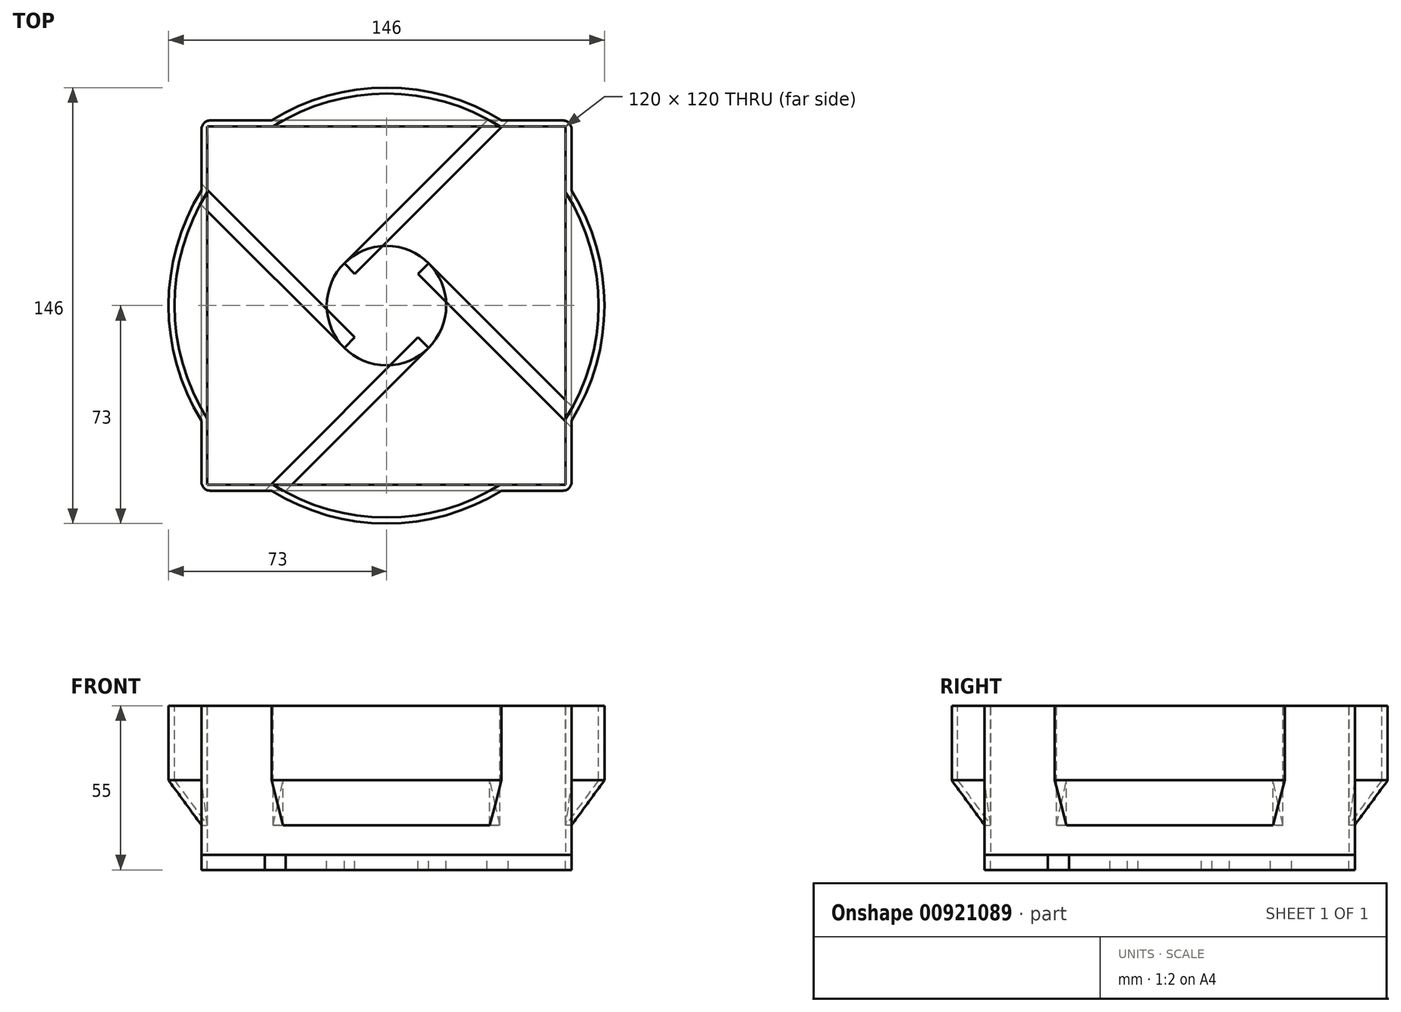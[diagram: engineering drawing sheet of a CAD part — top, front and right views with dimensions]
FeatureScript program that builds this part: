
annotation { "Feature Type Name" : "Feature", "Feature Type Description" : "" }
export const myFeature = defineFeature(function(context is Context, id is Id, definition is map)
    precondition{}
    {
        {
            var Q0;
            Q0=qCreatedBy(makeId("Top.planeOp"),FACE);
            var sketch = newSketch(context, id + "F0", { "sketchPlane" : qUnion([Q0])});
            skLineSegment(sketch, "E0.bottom", {"start": v(60, -60) * mm, "end": v(-60, -60) * mm});
            skLineSegment(sketch, "E0.top", {"start": v(60, 60) * mm, "end": v(-60, 60) * mm});
            skLineSegment(sketch, "E0.left", {"start": v(60, -60) * mm, "end": v(60, 60) * mm});
            skLineSegment(sketch, "E0.right", {"start": v(-60, -60) * mm, "end": v(-60, 60) * mm});
            skPoint(sketch, "E0.middle", {"position": v(0, 0) * mm});
            skLineSegment(sketch, "E1.bottom", {"start": v(62, -62) * mm, "end": v(-62, -62) * mm});
            skLineSegment(sketch, "E1.top", {"start": v(62, 62) * mm, "end": v(-62, 62) * mm});
            skLineSegment(sketch, "E1.left", {"start": v(62, -62) * mm, "end": v(62, 62) * mm});
            skLineSegment(sketch, "E1.right", {"start": v(-62, -62) * mm, "end": v(-62, 62) * mm});
            skCircle(sketch, "E2", {"center": v(0, 0) * mm, "radius": 20 * mm});
            skSolve(sketch);
        }
        {
            var Q0;
            Q0=makeQuery(id+"F0.imprint","IMPRINT",FACE,{"disambiguationData":[TD([[makeQuery(id+"F0.imprint","IMPRINT",EDGE,{"derivedFrom":sQuery(id+"F0.wireOp",EDGE,"E0.bottom")}),1.0]])]});
            extrude(context, id + "F1", {"entities" : qUnion([Q0]), "oppositeDirection" : true, "depth" : 5 * mm, "offsetDistance" : 25 * mm});
        }
        {
            var Q0;
            Q0=qCreatedBy(makeId("Top.planeOp"),FACE);
            var sketch = newSketch(context, id + "F2", { "sketchPlane" : qUnion([Q0])});
            skCircle(sketch, "E3", {"center": v(0, 0) * mm, "radius": 20 * mm});
            skSolve(sketch);
        }
        {
            var Q0;
            Q0=makeQuery(id+"F2.imprint","IMPRINT",FACE,{"disambiguationData":[TD([[makeQuery(id+"F2.imprint","IMPRINT",EDGE,{"derivedFrom":sQuery(id+"F2.wireOp",EDGE,"E3")}),1.0]])]});
            extrude(context, id + "F3", {"entities" : qUnion([Q0]), "oppositeDirection" : true, "depth" : 5 * mm, "offsetDistance" : 25 * mm});
        }
        {
            var Q0;
            Q0=qCreatedBy(makeId("Top.planeOp"),FACE);
            var sketch = newSketch(context, id + "F4", { "sketchPlane" : qUnion([Q0])});
            skLineSegment(sketch, "E4", {"start": v(0, 0) * mm, "end": v(-10.6, 10.6) * mm});
            skLineSegment(sketch, "E5", {"start": v(-10.6, 10.6) * mm, "end": v(-14.14, 14.14) * mm});
            skLineSegment(sketch, "E6", {"start": v(-14.14, 14.14) * mm, "end": v(33.72, 62) * mm});
            skLineSegment(sketch, "E7", {"start": v(-10.6, 10.6) * mm, "end": v(40.79, 62) * mm});
            skLineSegment(sketch, "E8", {"start": v(33.72, 62) * mm, "end": v(40.79, 62) * mm});
            skLineSegment(sketch, "E9.1.0", {"start": v(-14.14, -14.14) * mm, "end": v(-62, 33.72) * mm});
            skLineSegment(sketch, "E9.1.1", {"start": v(-62, 33.72) * mm, "end": v(-62, 40.79) * mm});
            skLineSegment(sketch, "E9.1.2", {"start": v(-10.6, -10.6) * mm, "end": v(-62, 40.79) * mm});
            skLineSegment(sketch, "E9.1.3", {"start": v(-10.6, -10.6) * mm, "end": v(-14.14, -14.14) * mm});
            skLineSegment(sketch, "E9.2.0", {"start": v(14.14, -14.14) * mm, "end": v(-33.72, -62) * mm});
            skLineSegment(sketch, "E9.2.1", {"start": v(-33.72, -62) * mm, "end": v(-40.79, -62) * mm});
            skLineSegment(sketch, "E9.2.2", {"start": v(10.6, -10.6) * mm, "end": v(-40.79, -62) * mm});
            skLineSegment(sketch, "E9.2.3", {"start": v(10.6, -10.6) * mm, "end": v(14.14, -14.14) * mm});
            skLineSegment(sketch, "E9.3.0", {"start": v(14.14, 14.14) * mm, "end": v(62, -33.72) * mm});
            skLineSegment(sketch, "E9.3.1", {"start": v(62, -33.72) * mm, "end": v(62, -40.79) * mm});
            skLineSegment(sketch, "E9.3.2", {"start": v(10.6, 10.6) * mm, "end": v(62, -40.79) * mm});
            skLineSegment(sketch, "E9.3.3", {"start": v(10.6, 10.6) * mm, "end": v(14.14, 14.14) * mm});
            skPoint(sketch, "E9.center", {"position": v(0, 0) * mm});
            skSolve(sketch);
        }
        {
            var Q0;
            Q0=makeQuery(id+"F4.imprint","IMPRINT",FACE,{"disambiguationData":[TD([[makeQuery(id+"F4.imprint","IMPRINT",EDGE,{"derivedFrom":sQuery(id+"F4.wireOp",EDGE,"E9.1.0")}),-1.0]])]});
            var Q1;
            Q1=makeQuery(id+"F4.imprint","IMPRINT",FACE,{"disambiguationData":[TD([[makeQuery(id+"F4.imprint","IMPRINT",EDGE,{"derivedFrom":sQuery(id+"F4.wireOp",EDGE,"E5")}),-1.0]])]});
            var Q2;
            Q2=makeQuery(id+"F4.imprint","IMPRINT",FACE,{"disambiguationData":[TD([[makeQuery(id+"F4.imprint","IMPRINT",EDGE,{"derivedFrom":sQuery(id+"F4.wireOp",EDGE,"E9.3.0")}),-1.0]])]});
            var Q3;
            Q3=makeQuery(id+"F4.imprint","IMPRINT",FACE,{"disambiguationData":[TD([[makeQuery(id+"F4.imprint","IMPRINT",EDGE,{"derivedFrom":sQuery(id+"F4.wireOp",EDGE,"E9.2.0")}),-1.0]])]});
            extrude(context, id + "F5", {"entities" : qUnion([Q0, Q1, Q2, Q3]), "oppositeDirection" : true, "depth" : 5 * mm, "offsetDistance" : 25 * mm});
        }
        {
            var Q0;
            Q0=makeQuery(id+"F1.opExtrude","CAP_FACE",FACE,{"disambiguationData":[OSD([sQuery(id+"F0.wireOp",EDGE,"E0.bottom"),sQuery(id+"F0.wireOp",EDGE,"E0.top"),sQuery(id+"F0.wireOp",EDGE,"E0.left"),sQuery(id+"F0.wireOp",EDGE,"E0.right"),sQuery(id+"F0.wireOp",EDGE,"E1.bottom"),sQuery(id+"F0.wireOp",EDGE,"E1.top"),sQuery(id+"F0.wireOp",EDGE,"E1.left"),sQuery(id+"F0.wireOp",EDGE,"E1.right")])],"isStart":true});
            extrude(context, id + "F6", {"entities" : qUnion([Q0]), "depth" : 50 * mm, "offsetDistance" : 25 * mm});
        }
        {
            var Q0;
            Q0=makeQuery(id+"F6.opExtrude","CAP_FACE",FACE,{"disambiguationData":[OSD([sQuery(id+"F0.wireOp",EDGE,"E0.bottom"),sQuery(id+"F0.wireOp",EDGE,"E0.top"),sQuery(id+"F0.wireOp",EDGE,"E0.left"),sQuery(id+"F0.wireOp",EDGE,"E0.right"),sQuery(id+"F0.wireOp",EDGE,"E1.bottom"),sQuery(id+"F0.wireOp",EDGE,"E1.top"),sQuery(id+"F0.wireOp",EDGE,"E1.left"),sQuery(id+"F0.wireOp",EDGE,"E1.right")])],"isStart":false});
            var sketch = newSketch(context, id + "F7", { "sketchPlane" : qUnion([Q0])});
            skCircle(sketch, "E10", {"center": v(0, 0) * mm, "radius": 71 * mm});
            skCircle(sketch, "E11", {"center": v(0, 0) * mm, "radius": 73 * mm});
            skLineSegment(sketch, "E12", {"start": v(34.6, -62) * mm, "end": v(-34.6, -62) * mm});
            skLineSegment(sketch, "E13", {"start": v(37.96, -60) * mm, "end": v(-37.96, -60) * mm});
            skLineSegment(sketch, "E14", {"start": v(60, -37.96) * mm, "end": v(60, 37.96) * mm});
            skLineSegment(sketch, "E15", {"start": v(62, -34.6) * mm, "end": v(62, 34.6) * mm});
            skLineSegment(sketch, "E16", {"start": v(37.96, 60) * mm, "end": v(-37.96, 60) * mm});
            skLineSegment(sketch, "E17", {"start": v(34.6, 62) * mm, "end": v(-34.6, 62) * mm});
            skLineSegment(sketch, "E18", {"start": v(-62, -34.6) * mm, "end": v(-62, 34.6) * mm});
            skLineSegment(sketch, "E19", {"start": v(-60, -37.96) * mm, "end": v(-60, 37.96) * mm});
            skLineSegment(sketch, "E20", {"start": v(-37.96, -60) * mm, "end": v(-41.58, -60) * mm});
            skLineSegment(sketch, "E21", {"start": v(-60, -37.96) * mm, "end": v(-60, -41.58) * mm});
            skLineSegment(sketch, "E22", {"start": v(-60, 41.58) * mm, "end": v(-60, 37.96) * mm});
            skLineSegment(sketch, "E23", {"start": v(-37.96, 60) * mm, "end": v(-41.58, 60) * mm});
            skLineSegment(sketch, "E24", {"start": v(37.96, -60) * mm, "end": v(41.58, -60) * mm});
            skLineSegment(sketch, "E25", {"start": v(60, -37.96) * mm, "end": v(60, -41.58) * mm});
            skLineSegment(sketch, "E26", {"start": v(60, 37.96) * mm, "end": v(60, 41.58) * mm});
            skLineSegment(sketch, "E27", {"start": v(37.96, 60) * mm, "end": v(41.58, 60) * mm});
            skSolve(sketch);
        }
        {
            var Q0;
            Q0 = qSketchRegion(id + "F7", true);
            extrude(context, id + "F8", {"entities" : qUnion([Q0]), "operationType" : NewBodyOperationType.ADD, "oppositeDirection" : true, "depth" : 25 * mm, "offsetDistance" : 25 * mm});
        }
        {
            var Q0;
            {var subQ0=sQuery(id+"F7.wireOp",EDGE,"E12");Q0=makeQuery(id+"F7.imprint","IMPRINT",FACE,{"disambiguationData":[TD([[makeQuery(id+"F7.imprint","IMPRINT",EDGE,{"derivedFrom":subQ0}),-1.0]])]});}
            var Q1;
            {var subQ0=sQuery(id+"F7.wireOp",EDGE,"E18");Q1=makeQuery(id+"F7.imprint","IMPRINT",FACE,{"disambiguationData":[TD([[makeQuery(id+"F7.imprint","IMPRINT",EDGE,{"derivedFrom":subQ0}),-1.0]])]});}
            var Q2;
            {var subQ0=sQuery(id+"F7.wireOp",EDGE,"E16");Q2=makeQuery(id+"F7.imprint","IMPRINT",FACE,{"disambiguationData":[TD([[makeQuery(id+"F7.imprint","IMPRINT",EDGE,{"derivedFrom":subQ0}),-1.0]])]});}
            var Q3;
            {var subQ0=sQuery(id+"F7.wireOp",EDGE,"E14");Q3=makeQuery(id+"F7.imprint","IMPRINT",FACE,{"disambiguationData":[TD([[makeQuery(id+"F7.imprint","IMPRINT",EDGE,{"derivedFrom":subQ0}),-1.0]])]});}
            extrude(context, id + "F9", {"entities" : qUnion([Q0, Q1, Q2, Q3]), "operationType" : NewBodyOperationType.REMOVE, "oppositeDirection" : true, "depth" : 25 * mm, "offsetDistance" : 25 * mm});
        }
        {
            var Q0;
            Q0=makeQuery(id+"F9.boolean.opBoolean","COPY",FACE,{"derivedFrom":makeQuery(id+"F9.opExtrude","CAP_FACE",FACE,{"disambiguationData":[OSD([sQuery(id+"F7.wireOp",EDGE,"E10"),sQuery(id+"F7.wireOp",EDGE,"E14"),sQuery(id+"F7.wireOp",EDGE,"E15")])],"isStart":false})});
            var Q1;
            Q1=makeQuery(id+"F9.boolean.opBoolean","COPY",FACE,{"derivedFrom":makeQuery(id+"F9.opExtrude","CAP_FACE",FACE,{"disambiguationData":[OSD([sQuery(id+"F7.wireOp",EDGE,"E10"),sQuery(id+"F7.wireOp",EDGE,"E12"),sQuery(id+"F7.wireOp",EDGE,"E13")])],"isStart":false})});
            var Q2;
            Q2=makeQuery(id+"F9.boolean.opBoolean","COPY",FACE,{"derivedFrom":makeQuery(id+"F9.opExtrude","CAP_FACE",FACE,{"disambiguationData":[OSD([sQuery(id+"F7.wireOp",EDGE,"E10"),sQuery(id+"F7.wireOp",EDGE,"E16"),sQuery(id+"F7.wireOp",EDGE,"E17")])],"isStart":false})});
            var Q3;
            Q3=makeQuery(id+"F9.boolean.opBoolean","COPY",FACE,{"derivedFrom":makeQuery(id+"F9.opExtrude","CAP_FACE",FACE,{"disambiguationData":[OSD([sQuery(id+"F7.wireOp",EDGE,"E10"),sQuery(id+"F7.wireOp",EDGE,"E18"),sQuery(id+"F7.wireOp",EDGE,"E19")])],"isStart":false})});
            extrude(context, id + "F10", {"entities" : qUnion([Q0, Q1, Q2, Q3]), "operationType" : NewBodyOperationType.REMOVE, "oppositeDirection" : true, "depth" : 15 * mm, "offsetDistance" : 25 * mm});
        }
        {
            var Q1;
            {var subQ0=sQuery(id+"F7.wireOp",EDGE,"E10");var subQ1=sQuery(id+"F7.wireOp",EDGE,"E11");Q1=makeQuery(id+"F8.boolean.opBoolean","SPLIT",FACE,{"disambiguationData":[TD([makeQuery(id+"F6.opExtrude","SWEPT_FACE",FACE,{"disambiguationData":[OSD([sQuery(id+"F0.wireOp",EDGE,"E1.top")])]}),makeQuery(id+"F8.opExtrude","SWEPT_FACE",FACE,{"disambiguationData":[OSD([subQ0])]}),makeQuery(id+"F8.opExtrude","SWEPT_FACE",FACE,{"disambiguationData":[OSD([subQ1])]})])],"derivedFrom":makeQuery(id+"F8.opExtrude","CAP_FACE",FACE,{"disambiguationData":[OSD([subQ0,subQ1])],"isStart":false})});}
            var Q2;
            Q2=makeQuery(id+"F10.boolean.opBoolean","COPY",FACE,{"derivedFrom":makeQuery(id+"F10.opExtrude","CAP_FACE",FACE,{"disambiguationData":[OSD([sQuery(id+"F7.wireOp",EDGE,"E10"),sQuery(id+"F7.wireOp",EDGE,"E16"),sQuery(id+"F7.wireOp",EDGE,"E17")])],"isStart":false})});
            loft(context, id + "F11", {"sheetProfilesArray" : [{ "sheetProfileEntities" : qUnion([Q1]) }, { "sheetProfileEntities" : qUnion([Q2]) }]});
        }
        {
            var Q1;
            Q1=makeQuery(id+"F10.boolean.opBoolean","COPY",FACE,{"derivedFrom":makeQuery(id+"F10.opExtrude","CAP_FACE",FACE,{"disambiguationData":[OSD([sQuery(id+"F7.wireOp",EDGE,"E10"),sQuery(id+"F7.wireOp",EDGE,"E18"),sQuery(id+"F7.wireOp",EDGE,"E19")])],"isStart":false})});
            var Q2;
            {var subQ0=sQuery(id+"F7.wireOp",EDGE,"E10");var subQ1=sQuery(id+"F7.wireOp",EDGE,"E11");Q2=makeQuery(id+"F8.boolean.opBoolean","SPLIT",FACE,{"disambiguationData":[TD([makeQuery(id+"F6.opExtrude","SWEPT_FACE",FACE,{"disambiguationData":[OSD([sQuery(id+"F0.wireOp",EDGE,"E1.right")])]}),makeQuery(id+"F8.opExtrude","SWEPT_FACE",FACE,{"disambiguationData":[OSD([subQ0])]}),makeQuery(id+"F8.opExtrude","SWEPT_FACE",FACE,{"disambiguationData":[OSD([subQ1])]})])],"derivedFrom":makeQuery(id+"F8.opExtrude","CAP_FACE",FACE,{"disambiguationData":[OSD([subQ0,subQ1])],"isStart":false})});}
            loft(context, id + "F12", {"sheetProfilesArray" : [{ "sheetProfileEntities" : qUnion([Q1]) }, { "sheetProfileEntities" : qUnion([Q2]) }]});
        }
        {
            var Q1;
            Q1=makeQuery(id+"F10.boolean.opBoolean","COPY",FACE,{"derivedFrom":makeQuery(id+"F10.opExtrude","CAP_FACE",FACE,{"disambiguationData":[OSD([sQuery(id+"F7.wireOp",EDGE,"E10"),sQuery(id+"F7.wireOp",EDGE,"E12"),sQuery(id+"F7.wireOp",EDGE,"E13")])],"isStart":false})});
            var Q2;
            {var subQ0=sQuery(id+"F7.wireOp",EDGE,"E10");var subQ1=sQuery(id+"F7.wireOp",EDGE,"E11");Q2=makeQuery(id+"F8.boolean.opBoolean","SPLIT",FACE,{"disambiguationData":[TD([makeQuery(id+"F6.opExtrude","SWEPT_FACE",FACE,{"disambiguationData":[OSD([sQuery(id+"F0.wireOp",EDGE,"E1.bottom")])]}),makeQuery(id+"F8.opExtrude","SWEPT_FACE",FACE,{"disambiguationData":[OSD([subQ0])]}),makeQuery(id+"F8.opExtrude","SWEPT_FACE",FACE,{"disambiguationData":[OSD([subQ1])]})])],"derivedFrom":makeQuery(id+"F8.opExtrude","CAP_FACE",FACE,{"disambiguationData":[OSD([subQ0,subQ1])],"isStart":false})});}
            loft(context, id + "F13", {"sheetProfilesArray" : [{ "sheetProfileEntities" : qUnion([Q1]) }, { "sheetProfileEntities" : qUnion([Q2]) }]});
        }
        {
            var Q1;
            {var subQ0=sQuery(id+"F7.wireOp",EDGE,"E11");var subQ1=sQuery(id+"F7.wireOp",EDGE,"E10");Q1=makeQuery(id+"F8.boolean.opBoolean","SPLIT",FACE,{"disambiguationData":[TD([makeQuery(id+"F6.opExtrude","SWEPT_FACE",FACE,{"disambiguationData":[OSD([sQuery(id+"F0.wireOp",EDGE,"E1.left")])]}),makeQuery(id+"F8.opExtrude","SWEPT_FACE",FACE,{"disambiguationData":[OSD([subQ1])]}),makeQuery(id+"F8.opExtrude","SWEPT_FACE",FACE,{"disambiguationData":[OSD([subQ0])]})])],"derivedFrom":makeQuery(id+"F8.opExtrude","CAP_FACE",FACE,{"disambiguationData":[OSD([subQ1,subQ0])],"isStart":false})});}
            var Q2;
            Q2=makeQuery(id+"F10.boolean.opBoolean","COPY",FACE,{"derivedFrom":makeQuery(id+"F10.opExtrude","CAP_FACE",FACE,{"disambiguationData":[OSD([sQuery(id+"F7.wireOp",EDGE,"E10"),sQuery(id+"F7.wireOp",EDGE,"E14"),sQuery(id+"F7.wireOp",EDGE,"E15")])],"isStart":false})});
            loft(context, id + "F14", {"sheetProfilesArray" : [{ "sheetProfileEntities" : qUnion([Q1]) }, { "sheetProfileEntities" : qUnion([Q2]) }]});
        }
        {
            var Q0;
            {var subQ0=sQuery(id+"F7.wireOp",EDGE,"E20");Q0=makeQuery(id+"F7.imprint","IMPRINT",FACE,{"disambiguationData":[TD([[makeQuery(id+"F7.imprint","IMPRINT",EDGE,{"derivedFrom":subQ0}),-1.0]])]});}
            extrude(context, id + "F15", {"entities" : qUnion([Q0]), "operationType" : NewBodyOperationType.REMOVE, "oppositeDirection" : true, "depth" : 25 * mm, "offsetDistance" : 25 * mm});
        }
        {
            var Q0;
            {var subQ2=sQuery(id+"F7.wireOp",EDGE,"E22");Q0=makeQuery(id+"F7.imprint","IMPRINT",FACE,{"disambiguationData":[TD([[makeQuery(id+"F7.imprint","IMPRINT",EDGE,{"derivedFrom":subQ2}),-1.0]])]});}
            extrude(context, id + "F16", {"entities" : qUnion([Q0]), "operationType" : NewBodyOperationType.REMOVE, "oppositeDirection" : true, "depth" : 25 * mm, "offsetDistance" : 25 * mm});
        }
        {
            var Q0;
            {var subQ0=sQuery(id+"F7.wireOp",EDGE,"E24");Q0=makeQuery(id+"F7.imprint","IMPRINT",FACE,{"disambiguationData":[TD([[makeQuery(id+"F7.imprint","IMPRINT",EDGE,{"derivedFrom":subQ0}),-1.0]])]});}
            extrude(context, id + "F17", {"entities" : qUnion([Q0]), "operationType" : NewBodyOperationType.REMOVE, "oppositeDirection" : true, "depth" : 25 * mm, "offsetDistance" : 25 * mm});
        }
        {
            var Q0;
            {var subQ0=sQuery(id+"F7.wireOp",EDGE,"E26");Q0=makeQuery(id+"F7.imprint","IMPRINT",FACE,{"disambiguationData":[TD([[makeQuery(id+"F7.imprint","IMPRINT",EDGE,{"derivedFrom":subQ0}),1.0]])]});}
            extrude(context, id + "F18", {"entities" : qUnion([Q0]), "operationType" : NewBodyOperationType.REMOVE, "oppositeDirection" : true, "depth" : 25 * mm, "offsetDistance" : 25 * mm});
        }
        {
            var Q0;
            Q0=makeQuery(id+"F6.opExtrude","SWEPT_EDGE",EDGE,{"disambiguationData":[OSD([sQuery(id+"F0.wireOp",EDGE,"E1.top"),sQuery(id+"F0.wireOp",EDGE,"E1.left")])]});
            var Q1;
            Q1=makeQuery(id+"F1.opExtrude","SWEPT_EDGE",EDGE,{"disambiguationData":[OSD([sQuery(id+"F0.wireOp",EDGE,"E1.top"),sQuery(id+"F0.wireOp",EDGE,"E1.left")])]});
            var Q2;
            Q2=makeQuery(id+"F6.opExtrude","SWEPT_EDGE",EDGE,{"disambiguationData":[OSD([sQuery(id+"F0.wireOp",EDGE,"E1.top"),sQuery(id+"F0.wireOp",EDGE,"E1.right")])]});
            var Q3;
            Q3=makeQuery(id+"F1.opExtrude","SWEPT_EDGE",EDGE,{"disambiguationData":[OSD([sQuery(id+"F0.wireOp",EDGE,"E1.top"),sQuery(id+"F0.wireOp",EDGE,"E1.right")])]});
            var Q4;
            Q4=makeQuery(id+"F6.opExtrude","SWEPT_EDGE",EDGE,{"disambiguationData":[OSD([sQuery(id+"F0.wireOp",EDGE,"E1.bottom"),sQuery(id+"F0.wireOp",EDGE,"E1.right")])]});
            var Q5;
            Q5=makeQuery(id+"F1.opExtrude","SWEPT_EDGE",EDGE,{"disambiguationData":[OSD([sQuery(id+"F0.wireOp",EDGE,"E1.bottom"),sQuery(id+"F0.wireOp",EDGE,"E1.right")])]});
            var Q6;
            Q6=makeQuery(id+"F6.opExtrude","SWEPT_EDGE",EDGE,{"disambiguationData":[OSD([sQuery(id+"F0.wireOp",EDGE,"E1.bottom"),sQuery(id+"F0.wireOp",EDGE,"E1.left")])]});
            var Q7;
            Q7=makeQuery(id+"F1.opExtrude","SWEPT_EDGE",EDGE,{"disambiguationData":[OSD([sQuery(id+"F0.wireOp",EDGE,"E1.bottom"),sQuery(id+"F0.wireOp",EDGE,"E1.left")])]});
            fillet(context, id + "F19", {"entities" : qUnion([Q0, Q1, Q2, Q3, Q4, Q5, Q6, Q7]), "radius" : 3 * mm, "tangentPropagation" : true, "allowEdgeOverflow" : false});
        }
    });
